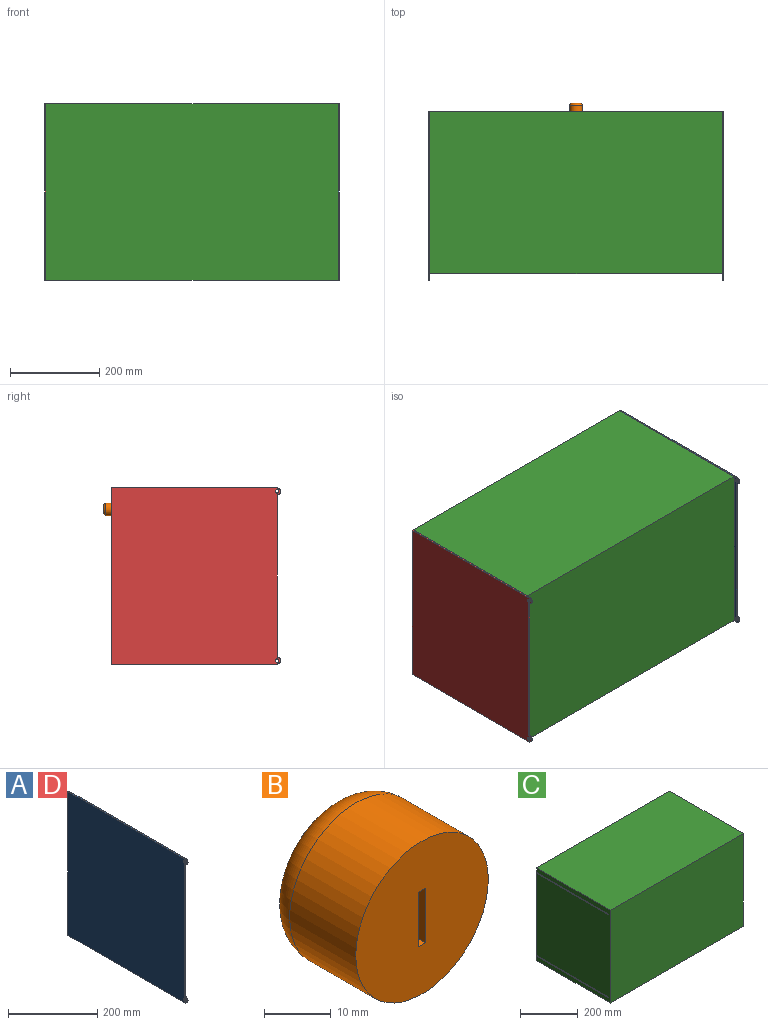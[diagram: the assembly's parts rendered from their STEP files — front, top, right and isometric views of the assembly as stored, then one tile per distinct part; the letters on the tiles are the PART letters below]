
ASSEMBLY  parts=4 mates=3
PART A: 10 faces, bbox 3.2x377.4x394.5 mm
  f0: cylinder r=7.87mm len=15.75mm, axis (-1,0,0), area 78.5mm2, adj f1,f7,f8,f9
  f1: plane 362.99x3.18mm, normal (0,-1,0), area 1152.5mm2, adj f0,f2,f8,f9
  f2: cylinder r=7.87mm len=15.75mm, axis (-1,0,0), area 78.5mm2, adj f1,f3,f8,f9
  f3: plane 369.49x3.18mm, normal (0,0,-1), area 1173.1mm2, adj f2,f4,f8,f9
  f4: plane 394.49x3.18mm, normal (0,1,0), area 1252.5mm2, adj f3,f7,f8,f9
  f5: cylinder r=4mm len=8mm, axis (-1,0,0), area 79.8mm2, adj f8,f9
  f6: cylinder r=4mm len=8mm, axis (-1,0,0), area 79.8mm2, adj f8,f9
  f7: plane 369.49x3.18mm, normal (0,0,1), area 1173.1mm2, adj f0,f4,f8,f9
  f8: plane 394.49x377.37mm, normal (1,0,0), area 145854.9mm2, adj f0,f1,f2,f3,f4,f5,f6,f7
  f9: plane 394.49x377.37mm, normal (-1,0,0), area 145854.9mm2, adj f0,f1,f2,f3,f4,f5,f6,f7
PART B: 8 faces, bbox 30.3x19.1x30.3 mm
  f0: plane 19.05x1.5mm, normal (0,0,1), area 28.6mm2, adj f1,f3,f5,f6
  f1: plane 19.05x10mm, normal (-1,0,0), area 190.5mm2, adj f0,f2,f5,f6
  f2: plane 19.05x1.5mm, normal (0,0,-1), area 28.6mm2, adj f1,f3,f5,f6
  f3: plane 19.05x10mm, normal (1,0,0), area 190.5mm2, adj f0,f2,f5,f6
  f4: cylinder r=14mm len=28mm, axis (0,-1,0), area 1228.9mm2, adj f6,f7
  f5: plane 17.84x17.84mm, normal (0,1,0), area 235mm2, adj f0,f1,f2,f3,f7
  f6: plane 28x28mm, normal (0,-1,0), area 600.8mm2, adj f0,f1,f2,f3,f4
  f7: torus R=8.92mm, axis (0,1,0), area 609.4mm2, adj f4,f5
PART C: 19 faces, bbox 654.1x362x394.5 mm
  f0: plane 654.05x349.91mm, normal (0,1,0), area 228857.6mm2, adj f2,f7,f8,f11
  f1: plane 654.05x18.82mm, normal (0,1,0), area 12312.1mm2, adj f2,f6,f7,f9
  f2: plane 394.49x361.95mm, normal (-1,0,0), area 140526.7mm2, adj f0,f1,f3,f4,f5,f6,f8,f9
  f3: plane 654.05x394.49mm, normal (0,-1,0), area 258014.5mm2, adj f2,f4,f6,f7
  f4: plane 654.05x361.95mm, normal (0,0,1), area 236733.4mm2, adj f2,f3,f5,f7
  f5: plane 654.05x19.4mm, normal (0,1,0), area 12691.6mm2, adj f2,f4,f7,f12
  f6: plane 654.05x361.95mm, normal (0,0,-1), area 236733.4mm2, adj f1,f2,f3,f7
  f7: plane 394.49x361.95mm, normal (1,0,0), area 140526.7mm2, adj f0,f1,f3,f4,f5,f6,f8,f9
  f8: plane 654.05x355.6mm, normal (0,0,-1), area 232580.2mm2, adj f0,f2,f7,f10
  f9: plane 654.05x355.6mm, normal (0,0,1), area 232580.2mm2, adj f1,f2,f7,f10
  f10: plane 654.05x3.18mm, normal (0,1,0), area 2076.6mm2, adj f2,f7,f8,f9
  f11: plane 654.05x355.6mm, normal (0,0,1), area 33104.8mm2, adj f0,f2,f7,f13,f14,f15,f16,f17
  f12: plane 654.05x355.6mm, normal (0,0,-1), area 232580.2mm2, adj f2,f5,f7,f13
  f13: plane 654.05x3.18mm, normal (0,1,0), area 2076.6mm2, adj f2,f7,f11,f12
  f14: plane 615.95x330.86mm, normal (0,-1,0), area 203792.2mm2, adj f11,f15,f17,f18
  f15: plane 330.86x323.85mm, normal (1,0,0), area 107148.5mm2, adj f11,f14,f16,f18
  f16: plane 615.95x330.86mm, normal (0,1,0), area 203792.2mm2, adj f11,f15,f17,f18
  f17: plane 330.86x323.85mm, normal (-1,0,0), area 107148.5mm2, adj f11,f14,f16,f18
  f18: plane 615.95x323.85mm, normal (0,0,1), area 199475.4mm2, adj f14,f15,f16,f17
PART D: same geometry as A
PLACE A t=(-4292.24,5964.03,-2170.54)mm
PLACE B t=(-5239.63,5964.03,-3175.76)mm
PLACE C t=(-3016.75,5964.03,-3176.96)mm
PLACE D t=(-4949.47,5964.03,-2170.54)mm
MATE revolute A.f9 <-> C.f7  axis (-1,0,0) through (-4292.24,-2201.47,760.47)mm
MATE fastened C.f0 <-> B.f6  axis (0,1,0) through (-4619.27,-2201.47,737.89)mm
MATE fastened D.f8 <-> C.f2  axis (1,0,0) through (-4946.29,-2201.47,760.47)mm
